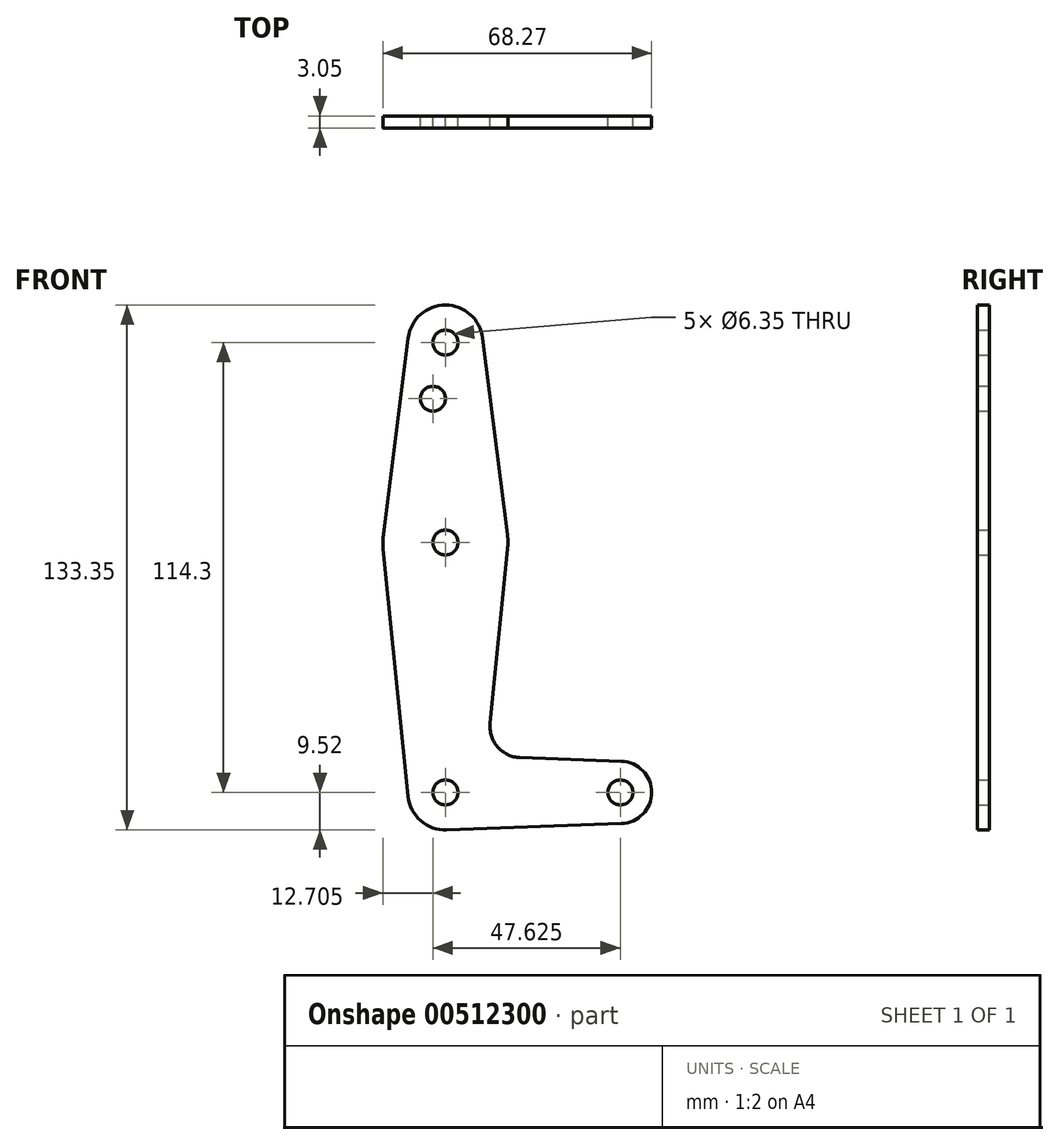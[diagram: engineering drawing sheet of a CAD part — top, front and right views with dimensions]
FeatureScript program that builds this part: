
annotation { "Feature Type Name" : "Feature", "Feature Type Description" : "" }
export const myFeature = defineFeature(function(context is Context, id is Id, definition is map)
    precondition{}
    {
        {
            var Q0;
            Q0=qCreatedBy(makeId("Front.planeOp"),FACE);
            var sketch = newSketch(context, id + "F0", { "sketchPlane" : qUnion([Q0])});
            skLineSegment(sketch, "E0", {"start": v(0, 114.3) * mm, "end": v(0, 0) * mm, "construction": true});
            skLineSegment(sketch, "E1", {"start": v(0, 0) * mm, "end": v(44.45, 0) * mm, "construction": true});
            skCircle(sketch, "E2", {"center": v(0, 114.3) * mm, "radius": 9.53 * mm});
            skCircle(sketch, "E3", {"center": v(0, 0) * mm, "radius": 9.53 * mm});
            skCircle(sketch, "E4", {"center": v(0, 63.5) * mm, "radius": 15.88 * mm});
            skCircle(sketch, "E5", {"center": v(44.45, 0) * mm, "radius": 7.94 * mm});
            skLineSegment(sketch, "E6", {"start": v(-9.45, 115.5) * mm, "end": v(-15.75, 65.48) * mm});
            skLineSegment(sketch, "E7", {"start": v(9.45, 115.5) * mm, "end": v(15.75, 65.48) * mm});
            skCircle(sketch, "E8", {"center": v(0, 114.3) * mm, "radius": 3.18 * mm});
            skCircle(sketch, "E9", {"center": v(0, 63.5) * mm, "radius": 3.18 * mm});
            skCircle(sketch, "E10", {"center": v(0, 0) * mm, "radius": 3.18 * mm});
            skCircle(sketch, "E11", {"center": v(44.45, 0) * mm, "radius": 3.18 * mm});
            skCircle(sketch, "E12", {"center": v(-3.17, 100.03) * mm, "radius": 3.18 * mm});
            skLineSegment(sketch, "E13", {"start": v(-15.8, 61.91) * mm, "end": v(-9.48, -0.95) * mm});
            skLineSegment(sketch, "E14", {"start": v(15.8, 61.91) * mm, "end": v(11.34, 17.6) * mm});
            skLineSegment(sketch, "E15", {"start": v(18.97, 8.85) * mm, "end": v(44.73, 7.93) * mm});
            skLineSegment(sketch, "E16", {"start": v(0.34, -9.52) * mm, "end": v(44.73, -7.93) * mm});
            skArc(sketch, "E17.filletArc", {"start": v(11.34, 17.6) * mm, "mid": v(13.26, 11.57) * mm, "end": v(18.97, 8.85) * mm});
            skSolve(sketch);
        }
        {
            var Q0;
            Q0 = qSketchRegion(id + "F0", true);
            extrude(context, id + "F1", {"entities" : qUnion([Q0]), "depth" : 3.05 * mm});
        }
    });
